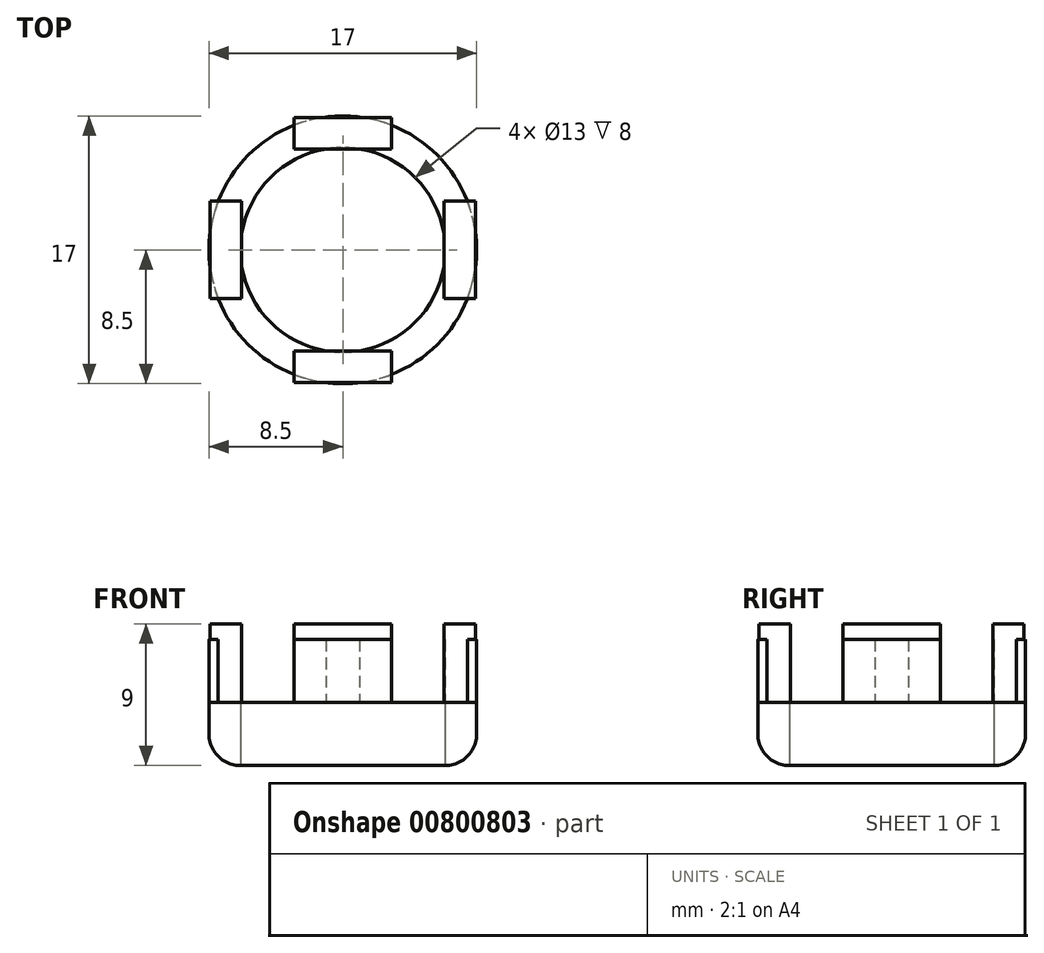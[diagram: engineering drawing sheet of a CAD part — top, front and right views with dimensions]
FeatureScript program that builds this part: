
annotation { "Feature Type Name" : "Feature", "Feature Type Description" : "" }
export const myFeature = defineFeature(function(context is Context, id is Id, definition is map)
    precondition{}
    {
        {
            var Q0;
            Q0=qCreatedBy(makeId("Top.planeOp"),FACE);
            var sketch = newSketch(context, id + "F0", { "sketchPlane" : qUnion([Q0])});
            skLineSegment(sketch, "E0", {"start": v(0, 0) * mm, "end": v(6.5, 0) * mm, "construction": true});
            skCircle(sketch, "E1", {"center": v(0, 0) * mm, "radius": 6.5 * mm});
            skLineSegment(sketch, "E2", {"start": v(6.5, 0) * mm, "end": v(8.5, 0) * mm, "construction": true});
            skCircle(sketch, "E3", {"center": v(0, 0) * mm, "radius": 8.5 * mm});
            skSolve(sketch);
        }
        {
            var Q0;
            Q0=makeQuery(id+"F0.imprint","IMPRINT",FACE,{"disambiguationData":[TD([[makeQuery(id+"F0.imprint","IMPRINT",EDGE,{"derivedFrom":sQuery(id+"F0.wireOp",EDGE,"E1")}),-1.0]])]});
            extrude(context, id + "F1", {"entities" : qUnion([Q0]), "depth" : 4 * mm, "offsetDistance" : 25 * mm});
        }
        {
            var Q0;
            Q0=makeQuery(id+"F1.opExtrude","CAP_EDGE",EDGE,{"disambiguationData":[OSD([sQuery(id+"F0.wireOp",EDGE,"E3")])],"isStart":true});
            fillet(context, id + "F2", {"entities" : qUnion([Q0]), "radius" : 2 * mm, "tangentPropagation" : true, "allowEdgeOverflow" : false});
        }
        {
            var Q0;
            Q0=makeQuery(id+"F1.opExtrude","CAP_FACE",FACE,{"disambiguationData":[OSD([sQuery(id+"F0.wireOp",EDGE,"E1"),sQuery(id+"F0.wireOp",EDGE,"E3")])],"isStart":false});
            var sketch = newSketch(context, id + "F3", { "sketchPlane" : qUnion([Q0])});
            skLineSegment(sketch, "E4.bottom", {"start": v(0, -6.5) * mm, "end": v(0, -6.5) * mm});
            skLineSegment(sketch, "E4.top", {"start": v(0, -8.5) * mm, "end": v(0, -8.5) * mm});
            skLineSegment(sketch, "E4.left", {"start": v(0, -6.5) * mm, "end": v(0, -8.5) * mm, "construction": true});
            skLineSegment(sketch, "E4.right", {"start": v(0, -6.5) * mm, "end": v(0, -8.5) * mm, "construction": true});
            skLineSegment(sketch, "E5.bottom", {"start": v(-3.1, -6.41) * mm, "end": v(3.1, -6.41) * mm, "construction": true});
            skLineSegment(sketch, "E5.top", {"start": v(-3.1, -8.59) * mm, "end": v(3.1, -8.59) * mm, "construction": true});
            skLineSegment(sketch, "E5.left", {"start": v(-3.1, -6.41) * mm, "end": v(-3.1, -8.59) * mm, "construction": true});
            skLineSegment(sketch, "E5.right", {"start": v(3.1, -6.41) * mm, "end": v(3.1, -8.59) * mm, "construction": true});
            skPoint(sketch, "E5.middle", {"position": v(0, -7.5) * mm});
            skLineSegment(sketch, "E6", {"start": v(0, -8.5) * mm, "end": v(0, 8.5) * mm, "construction": true});
            skLineSegment(sketch, "E7", {"start": v(0, 8.5) * mm, "end": v(0, 0) * mm, "construction": true});
            skLineSegment(sketch, "E8", {"start": v(0, 0) * mm, "end": v(8.5, 0) * mm, "construction": true});
            skLineSegment(sketch, "E9", {"start": v(0, 0) * mm, "end": v(-8.5, 0) * mm, "construction": true});
            skLineSegment(sketch, "E10.bottom", {"start": v(-3.1, -6.41) * mm, "end": v(3.1, -6.41) * mm});
            skLineSegment(sketch, "E10.top", {"start": v(-3.1, -8.59) * mm, "end": v(3.1, -8.59) * mm});
            skLineSegment(sketch, "E10.left", {"start": v(-3.1, -6.41) * mm, "end": v(-3.1, -8.59) * mm});
            skLineSegment(sketch, "E10.right", {"start": v(3.1, -6.41) * mm, "end": v(3.1, -8.59) * mm});
            skSolve(sketch);
        }
        {
            var Q0;
            Q0=makeQuery(id+"F3.imprint","IMPRINT",FACE,{"disambiguationData":[TD([[makeQuery(id+"F3.imprint","IMPRINT",EDGE,{"derivedFrom":sQuery(id+"F3.wireOp",EDGE,"E10.bottom")}),-1.0]])]});
            extrude(context, id + "F4", {"entities" : qUnion([Q0]), "operationType" : NewBodyOperationType.ADD, "depth" : 4 * mm, "offsetDistance" : 25 * mm});
        }
        {
            var Q0;
            Q0=makeQuery(id+"F4.opExtrude","CAP_FACE",FACE,{"disambiguationData":[OSD([sQuery(id+"F3.wireOp",EDGE,"E10.bottom"),sQuery(id+"F3.wireOp",EDGE,"E10.top"),sQuery(id+"F3.wireOp",EDGE,"E10.left"),sQuery(id+"F3.wireOp",EDGE,"E10.right")])],"isStart":false});
            var sketch = newSketch(context, id + "F5", { "sketchPlane" : qUnion([Q0])});
            skLineSegment(sketch, "E11.bottom", {"start": v(3.1, -6.41) * mm, "end": v(-3.1, -6.41) * mm});
            skLineSegment(sketch, "E11.top", {"start": v(3.1, -8.41) * mm, "end": v(-3.1, -8.41) * mm});
            skLineSegment(sketch, "E11.left", {"start": v(3.1, -6.41) * mm, "end": v(3.1, -8.41) * mm});
            skLineSegment(sketch, "E11.right", {"start": v(-3.1, -6.41) * mm, "end": v(-3.1, -8.41) * mm});
            skSolve(sketch);
        }
        {
            var Q0;
            Q0 = qSketchRegion(id + "F5", true);
            extrude(context, id + "F6", {"entities" : qUnion([Q0]), "operationType" : NewBodyOperationType.ADD, "depth" : 1 * mm, "offsetDistance" : 25 * mm});
        }
        {
            var Q0;
            Q0=qCreatedBy(makeId("Front.planeOp"),FACE);
            var sketch = newSketch(context, id + "F7", { "sketchPlane" : qUnion([Q0])});
            skLineSegment(sketch, "E12", {"start": v(0, 0) * mm, "end": v(0, 20.57) * mm, "construction": true});
            skSolve(sketch);
        }
        {
            var Q0;
            Q0=makeQuery(id+"F1.opExtrude","SWEPT_BODY",BODY,{"disambiguationData":[OSD([sQuery(id+"F0.wireOp",EDGE,"E1"),sQuery(id+"F0.wireOp",EDGE,"E3")])]});
            var Q1;
            Q1=sQuery(id+"F7.wireOp",EDGE,"E12");
            circularPattern(context, id + "F8", {"entities" : qUnion([Q0]), "axis" : qUnion([Q1]), "angle" : 360 * degree, "instanceCount" : 4, "equalSpace" : true});
        }
    });
